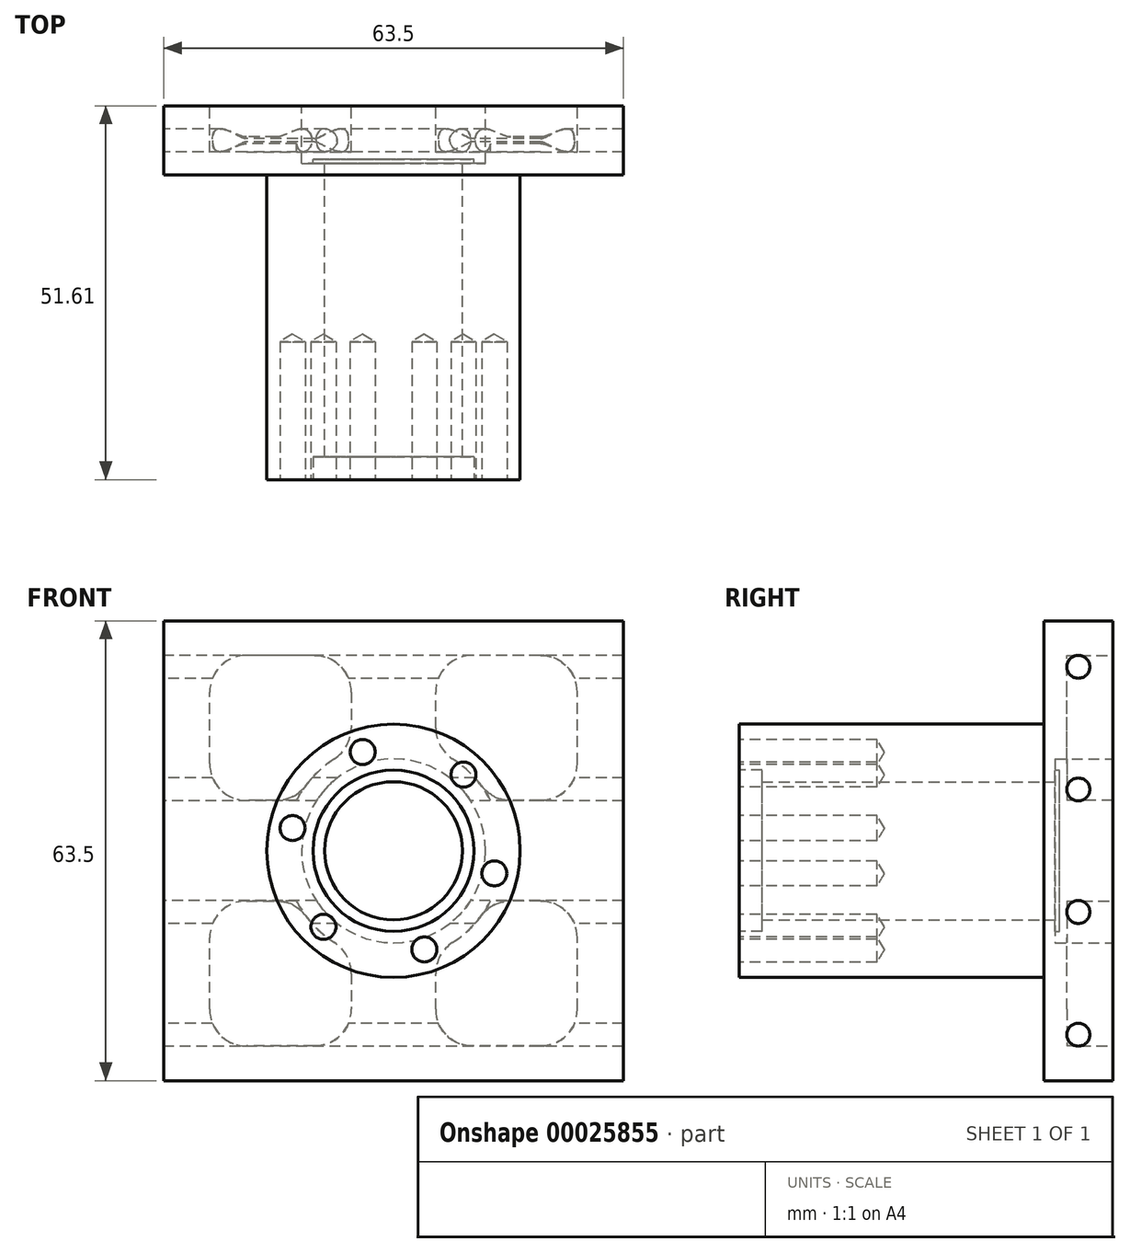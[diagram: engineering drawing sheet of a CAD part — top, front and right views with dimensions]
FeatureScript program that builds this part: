
annotation { "Feature Type Name" : "Feature", "Feature Type Description" : "" }
export const myFeature = defineFeature(function(context is Context, id is Id, definition is map)
    precondition{}
    {
        {
            var Q0;
            Q0=qCreatedBy(makeId("Front.planeOp"),FACE);
            var sketch = newSketch(context, id + "F0", { "sketchPlane" : qUnion([Q0])});
            skLineSegment(sketch, "E0.rect.bottom", {"start": v(31.75, -31.75) * mm, "end": v(-31.75, -31.75) * mm});
            skLineSegment(sketch, "E0.rect.top", {"start": v(31.75, 31.75) * mm, "end": v(-31.75, 31.75) * mm});
            skLineSegment(sketch, "E0.rect.left", {"start": v(31.75, -31.75) * mm, "end": v(31.75, 31.75) * mm});
            skLineSegment(sketch, "E0.rect.right", {"start": v(-31.75, -31.75) * mm, "end": v(-31.75, 31.75) * mm});
            skPoint(sketch, "E0.rect.middle", {"position": v(0, 0) * mm});
            skSolve(sketch);
        }
        {
            var Q0;
            Q0=makeQuery(id+"F0.imprint","IMPRINT",FACE,{"disambiguationData":[TD([[makeQuery(id+"F0.imprint","IMPRINT",EDGE,{"derivedFrom":sQuery(id+"F0.wireOp",EDGE,"E0.rect.bottom")}),-1.0]])]});
            extrude(context, id + "F1", {"entities" : qUnion([Q0]), "depth" : 9.52 * mm});
        }
        {
            var Q0;
            Q0=makeQuery(id+"F1.opExtrude","SWEPT_FACE",FACE,{"disambiguationData":[OSD([sQuery(id+"F0.wireOp",EDGE,"E0.rect.right")])]});
            var sketch = newSketch(context, id + "F2", { "sketchPlane" : qUnion([Q0])});
            skLineSegment(sketch, "E1", {"start": v(4.75, 47.41) * mm, "end": v(4.75, -43.38) * mm});
            skPoint(sketch, "E2", {"position": v(4.75, 25.4) * mm});
            skPoint(sketch, "E3", {"position": v(4.75, 8.46) * mm});
            skPoint(sketch, "E4", {"position": v(4.75, -8.46) * mm});
            skPoint(sketch, "E5", {"position": v(4.75, -25.4) * mm});
            skSolve(sketch);
        }
        {
            var Q0;
            Q0=sQuery(id+"F2.wireOp",VERTEX,"E2");
            var Q1;
            Q1=sQuery(id+"F2.wireOp",VERTEX,"E3");
            var Q2;
            Q2=sQuery(id+"F2.wireOp",VERTEX,"E4");
            var Q3;
            Q3=sQuery(id+"F2.wireOp",VERTEX,"E5");
            var Q4;
            Q4=makeQuery(id+"F1.opExtrude","SWEPT_BODY",BODY,{"disambiguationData":[OSD([sQuery(id+"F0.wireOp",EDGE,"E0.rect.bottom"),sQuery(id+"F0.wireOp",EDGE,"E0.rect.top"),sQuery(id+"F0.wireOp",EDGE,"E0.rect.left"),sQuery(id+"F0.wireOp",EDGE,"E0.rect.right")])]});
            hole(context, id + "F3", {"style" : HoleStyle.SIMPLE, "holeDiameter" : 3.17 * mm, "endStyle" : HoleEndStyle.THROUGH, "locations" : qUnion([Q0, Q1, Q2, Q3]), "scope" : qUnion([Q4])});
        }
        {
            var Q0;
            Q0=makeQuery(id+"F1.opExtrude","CAP_FACE",FACE,{"disambiguationData":[OSD([sQuery(id+"F0.wireOp",EDGE,"E0.rect.bottom"),sQuery(id+"F0.wireOp",EDGE,"E0.rect.top"),sQuery(id+"F0.wireOp",EDGE,"E0.rect.left"),sQuery(id+"F0.wireOp",EDGE,"E0.rect.right")])],"isStart":false});
            var sketch = newSketch(context, id + "F4", { "sketchPlane" : qUnion([Q0])});
            skCircle(sketch, "E6", {"center": v(0, 0) * mm, "radius": 17.49 * mm});
            skSolve(sketch);
        }
        {
            var Q0;
            Q0=makeQuery(id+"F4.imprint","IMPRINT",FACE,{"disambiguationData":[TD([[makeQuery(id+"F4.imprint","IMPRINT",EDGE,{"derivedFrom":sQuery(id+"F4.wireOp",EDGE,"E6")}),1.0]])]});
            extrude(context, id + "F5", {"entities" : qUnion([Q0]), "operationType" : NewBodyOperationType.ADD, "depth" : 42.1 * mm});
        }
        {
            var Q0;
            Q0=makeQuery(id+"F5.opExtrude","CAP_FACE",FACE,{"disambiguationData":[OSD([sQuery(id+"F4.wireOp",EDGE,"E6")])],"isStart":false});
            var sketch = newSketch(context, id + "F6", { "sketchPlane" : qUnion([Q0])});
            skCircle(sketch, "E7", {"center": v(0, 0) * mm, "radius": 14.29 * mm});
            skCircle(sketch, "E8.cCircle", {"center": v(0, 0) * mm, "radius": 14.29 * mm, "construction": true});
            skLineSegment(sketch, "E8.0", {"start": v(9.68, 10.51) * mm, "end": v(13.94, -3.12) * mm});
            skLineSegment(sketch, "E8.1", {"start": v(13.94, -3.12) * mm, "end": v(4.27, -13.64) * mm});
            skLineSegment(sketch, "E8.2", {"start": v(4.27, -13.64) * mm, "end": v(-9.68, -10.51) * mm});
            skLineSegment(sketch, "E8.3", {"start": v(-9.68, -10.51) * mm, "end": v(-13.94, 3.12) * mm});
            skLineSegment(sketch, "E8.4", {"start": v(-13.94, 3.12) * mm, "end": v(-4.27, 13.64) * mm});
            skLineSegment(sketch, "E8.5", {"start": v(-4.27, 13.64) * mm, "end": v(9.68, 10.51) * mm});
            skSolve(sketch);
        }
        {
            var Q0;
            Q0=sQuery(id+"F6.wireOp",VERTEX,"E8.3.end");
            var Q1;
            Q1=sQuery(id+"F6.wireOp",VERTEX,"E8.4.end");
            var Q2;
            Q2=sQuery(id+"F6.wireOp",VERTEX,"E8.0.start");
            var Q3;
            Q3=sQuery(id+"F6.wireOp",VERTEX,"E8.1.start");
            var Q4;
            Q4=sQuery(id+"F6.wireOp",VERTEX,"E8.2.start");
            var Q5;
            Q5=sQuery(id+"F6.wireOp",VERTEX,"E8.3.start");
            var Q6;
            Q6=makeQuery(id+"F1.opExtrude","SWEPT_BODY",BODY,{"disambiguationData":[OSD([sQuery(id+"F0.wireOp",EDGE,"E0.rect.bottom"),sQuery(id+"F0.wireOp",EDGE,"E0.rect.top"),sQuery(id+"F0.wireOp",EDGE,"E0.rect.left"),sQuery(id+"F0.wireOp",EDGE,"E0.rect.right")])]});
            hole(context, id + "F7", {"style" : HoleStyle.SIMPLE, "holeDiameter" : 3.45 * mm, "endStyle" : HoleEndStyle.BLIND, "holeDepth" : 19.05 * mm, "locations" : qUnion([Q0, Q1, Q2, Q3, Q4, Q5]), "scope" : qUnion([Q6])});
        }
        {
            var Q0;
            Q0=makeQuery(id+"F1.opExtrude","CAP_FACE",FACE,{"disambiguationData":[OSD([sQuery(id+"F0.wireOp",EDGE,"E0.rect.bottom"),sQuery(id+"F0.wireOp",EDGE,"E0.rect.top"),sQuery(id+"F0.wireOp",EDGE,"E0.rect.left"),sQuery(id+"F0.wireOp",EDGE,"E0.rect.right")])],"isStart":true});
            var sketch = newSketch(context, id + "F8", { "sketchPlane" : qUnion([Q0])});
            skCircle(sketch, "E9", {"center": v(0, 0) * mm, "radius": 12.7 * mm});
            skCircle(sketch, "E10", {"center": v(0, 0) * mm, "radius": 11.13 * mm});
            skCircle(sketch, "E11", {"center": v(0, 0) * mm, "radius": 9.53 * mm});
            skSolve(sketch);
        }
        {
            var Q0;
            Q0=makeQuery(id+"F8.imprint","IMPRINT",FACE,{"disambiguationData":[TD([[makeQuery(id+"F8.imprint","IMPRINT",EDGE,{"derivedFrom":sQuery(id+"F8.wireOp",EDGE,"E11")}),1.0]])]});
            extrude(context, id + "F9", {"entities" : qUnion([Q0]), "operationType" : NewBodyOperationType.REMOVE, "endBound" : BoundingType.THROUGH_ALL, "oppositeDirection" : true, "depth" : 25.4 * mm});
        }
        {
            var Q0;
            Q0=qCreatedBy(makeId("Front.planeOp"),FACE);
            var sketch = newSketch(context, id + "F10", { "sketchPlane" : qUnion([Q0])});
            skCircle(sketch, "E12", {"center": v(0, 0) * mm, "radius": 11.13 * mm});
            skCircle(sketch, "E13", {"center": v(0, 0) * mm, "radius": 12.7 * mm});
            skSolve(sketch);
        }
        {
            var Q0;
            Q0=makeQuery(id+"F10.imprint","IMPRINT",FACE,{"disambiguationData":[TD([[makeQuery(id+"F10.imprint","IMPRINT",EDGE,{"derivedFrom":sQuery(id+"F10.wireOp",EDGE,"E12")}),1.0]])]});
            extrude(context, id + "F11", {"entities" : qUnion([Q0]), "operationType" : NewBodyOperationType.REMOVE, "depth" : 7.37 * mm});
        }
        {
            var Q0;
            Q0=makeQuery(id+"F1.opExtrude","CAP_FACE",FACE,{"disambiguationData":[OSD([sQuery(id+"F0.wireOp",EDGE,"E0.rect.bottom"),sQuery(id+"F0.wireOp",EDGE,"E0.rect.top"),sQuery(id+"F0.wireOp",EDGE,"E0.rect.left"),sQuery(id+"F0.wireOp",EDGE,"E0.rect.right")])],"isStart":true});
            var sketch = newSketch(context, id + "F12", { "sketchPlane" : qUnion([Q0])});
            skCircle(sketch, "E14", {"center": v(0, 0) * mm, "radius": 12.7 * mm});
            skSolve(sketch);
        }
        {
            var Q0;
            Q0=makeQuery(id+"F12.imprint","IMPRINT",FACE,{"disambiguationData":[TD([[makeQuery(id+"F12.imprint","IMPRINT",EDGE,{"derivedFrom":sQuery(id+"F12.wireOp",EDGE,"E14")}),1.0]])]});
            extrude(context, id + "F13", {"entities" : qUnion([Q0]), "operationType" : NewBodyOperationType.REMOVE, "oppositeDirection" : true, "depth" : 7.95 * mm});
        }
        {
            var Q0;
            Q0=makeQuery(id+"F5.opExtrude","CAP_FACE",FACE,{"disambiguationData":[OSD([sQuery(id+"F4.wireOp",EDGE,"E6")])],"isStart":false});
            var sketch = newSketch(context, id + "F14", { "sketchPlane" : qUnion([Q0])});
            skCircle(sketch, "E15", {"center": v(0, 0) * mm, "radius": 11.13 * mm});
            skSolve(sketch);
        }
        {
            var Q0;
            Q0=makeQuery(id+"F14.imprint","IMPRINT",FACE,{"disambiguationData":[TD([[makeQuery(id+"F14.imprint","IMPRINT",EDGE,{"derivedFrom":sQuery(id+"F14.wireOp",EDGE,"E15")}),1.0]])]});
            extrude(context, id + "F15", {"entities" : qUnion([Q0]), "operationType" : NewBodyOperationType.REMOVE, "oppositeDirection" : true, "depth" : 3.17 * mm});
        }
        {
            var Q0;
            Q0=makeQuery(id+"F1.opExtrude","CAP_FACE",FACE,{"disambiguationData":[OSD([sQuery(id+"F0.wireOp",EDGE,"E0.rect.bottom"),sQuery(id+"F0.wireOp",EDGE,"E0.rect.top"),sQuery(id+"F0.wireOp",EDGE,"E0.rect.left"),sQuery(id+"F0.wireOp",EDGE,"E0.rect.right")])],"isStart":true});
            var sketch = newSketch(context, id + "F16", { "sketchPlane" : qUnion([Q0])});
            skLineSegment(sketch, "E16.rect.bottom", {"start": v(-25.4, -26.97) * mm, "end": v(25.4, -26.97) * mm});
            skLineSegment(sketch, "E16.rect.top", {"start": v(-25.4, 26.97) * mm, "end": v(25.4, 26.97) * mm});
            skLineSegment(sketch, "E16.rect.left", {"start": v(-25.4, -26.97) * mm, "end": v(-25.4, 26.97) * mm});
            skLineSegment(sketch, "E16.rect.right", {"start": v(25.4, -26.97) * mm, "end": v(25.4, 26.97) * mm});
            skPoint(sketch, "E16.rect.middle", {"position": v(0, 0) * mm});
            skCircle(sketch, "E17", {"center": v(0, 0) * mm, "radius": 15.09 * mm});
            skLineSegment(sketch, "E18", {"start": v(34.8, 0) * mm, "end": v(-37.6, 0) * mm});
            skLineSegment(sketch, "E19", {"start": v(25.4, 6.94) * mm, "end": v(13.4, 6.94) * mm});
            skLineSegment(sketch, "E20", {"start": v(25.4, -6.94) * mm, "end": v(13.4, -6.94) * mm});
            skLineSegment(sketch, "E21", {"start": v(-5.83, -26.97) * mm, "end": v(-5.83, -13.91) * mm});
            skLineSegment(sketch, "E22", {"start": v(5.83, 26.97) * mm, "end": v(5.83, 13.91) * mm});
            skPoint(sketch, "E23.start.orphan", {"position": v(0, -38.63) * mm});
            skLineSegment(sketch, "E24.trimOffspring", {"start": v(5.83, -13.91) * mm, "end": v(5.83, -26.97) * mm});
            skLineSegment(sketch, "E25.trimOffspring", {"start": v(-13.4, -6.94) * mm, "end": v(-25.4, -6.94) * mm});
            skLineSegment(sketch, "E26.trimOffspring", {"start": v(-13.4, 6.94) * mm, "end": v(-25.4, 6.94) * mm});
            skLineSegment(sketch, "E27.trimOffspring", {"start": v(-5.83, 13.91) * mm, "end": v(-5.83, 26.97) * mm});
            skSolve(sketch);
        }
        {
            var Q0;
            {var subQ1=sQuery(id+"F16.wireOp",EDGE,"E26.trimOffspring");Q0=makeQuery(id+"F16.imprint","IMPRINT",FACE,{"disambiguationData":[TD([[makeQuery(id+"F16.imprint","IMPRINT",EDGE,{"derivedFrom":subQ1}),-1.0]])]});}
            var Q1;
            {var subQ1=sQuery(id+"F16.wireOp",EDGE,"E21");Q1=makeQuery(id+"F16.imprint","IMPRINT",FACE,{"disambiguationData":[TD([[makeQuery(id+"F16.imprint","IMPRINT",EDGE,{"derivedFrom":subQ1}),1.0]])]});}
            var Q2;
            {var subQ0=sQuery(id+"F16.wireOp",EDGE,"E20");Q2=makeQuery(id+"F16.imprint","IMPRINT",FACE,{"disambiguationData":[TD([[makeQuery(id+"F16.imprint","IMPRINT",EDGE,{"derivedFrom":subQ0}),1.0]])]});}
            var Q3;
            {var subQ1=sQuery(id+"F16.wireOp",EDGE,"E19");Q3=makeQuery(id+"F16.imprint","IMPRINT",FACE,{"disambiguationData":[TD([[makeQuery(id+"F16.imprint","IMPRINT",EDGE,{"derivedFrom":subQ1}),-1.0]])]});}
            extrude(context, id + "F17", {"entities" : qUnion([Q0, Q1, Q2, Q3]), "operationType" : NewBodyOperationType.REMOVE, "oppositeDirection" : true, "depth" : 6.35 * mm});
        }
        {
            var Q0;
            {var subQ0=sQuery(id+"F16.wireOp",EDGE,"E16.rect.bottom");var subQ1=sQuery(id+"F16.wireOp",EDGE,"E24.trimOffspring");Q0=makeQuery(id+"F17.boolean.opBoolean","COPY",EDGE,{"disambiguationData":[TD([makeQuery(id+"F1.opExtrude","CAP_FACE",FACE,{"disambiguationData":[OSD([sQuery(id+"F0.wireOp",EDGE,"E0.rect.bottom"),sQuery(id+"F0.wireOp",EDGE,"E0.rect.top"),sQuery(id+"F0.wireOp",EDGE,"E0.rect.left"),sQuery(id+"F0.wireOp",EDGE,"E0.rect.right")])],"isStart":true})])],"derivedFrom":makeQuery(id+"F17.opExtrude","SWEPT_EDGE",EDGE,{"disambiguationData":[OSD([subQ0,subQ1])]})});}
            var Q1;
            {var subQ0=sQuery(id+"F16.wireOp",EDGE,"E16.rect.left");var subQ1=sQuery(id+"F16.wireOp",EDGE,"E16.rect.bottom");Q1=makeQuery(id+"F17.boolean.opBoolean","COPY",EDGE,{"disambiguationData":[TD([makeQuery(id+"F1.opExtrude","CAP_FACE",FACE,{"disambiguationData":[OSD([sQuery(id+"F0.wireOp",EDGE,"E0.rect.bottom"),sQuery(id+"F0.wireOp",EDGE,"E0.rect.top"),sQuery(id+"F0.wireOp",EDGE,"E0.rect.left"),sQuery(id+"F0.wireOp",EDGE,"E0.rect.right")])],"isStart":true})])],"derivedFrom":makeQuery(id+"F17.opExtrude","SWEPT_EDGE",EDGE,{"disambiguationData":[OSD([subQ1,subQ0])]})});}
            var Q2;
            {var subQ0=sQuery(id+"F16.wireOp",EDGE,"E26.trimOffspring");var subQ1=sQuery(id+"F16.wireOp",EDGE,"E16.rect.left");Q2=makeQuery(id+"F17.boolean.opBoolean","COPY",EDGE,{"disambiguationData":[TD([makeQuery(id+"F1.opExtrude","CAP_FACE",FACE,{"disambiguationData":[OSD([sQuery(id+"F0.wireOp",EDGE,"E0.rect.bottom"),sQuery(id+"F0.wireOp",EDGE,"E0.rect.top"),sQuery(id+"F0.wireOp",EDGE,"E0.rect.left"),sQuery(id+"F0.wireOp",EDGE,"E0.rect.right")])],"isStart":true})])],"derivedFrom":makeQuery(id+"F17.opExtrude","SWEPT_EDGE",EDGE,{"disambiguationData":[OSD([subQ1,subQ0])]})});}
            var Q3;
            Q3=makeQuery(id+"F17.boolean.opBoolean","COPY",EDGE,{"derivedFrom":makeQuery(id+"F17.opExtrude","SWEPT_EDGE",EDGE,{"disambiguationData":[OSD([sQuery(id+"F16.wireOp",EDGE,"E17"),sQuery(id+"F16.wireOp",EDGE,"E22")])]})});
            var Q4;
            {var subQ0=sQuery(id+"F16.wireOp",EDGE,"E19");var subQ1=sQuery(id+"F16.wireOp",EDGE,"E17");Q4=makeQuery(id+"F17.boolean.opBoolean","COPY",EDGE,{"disambiguationData":[TD([makeQuery(id+"F1.opExtrude","CAP_FACE",FACE,{"disambiguationData":[OSD([sQuery(id+"F0.wireOp",EDGE,"E0.rect.bottom"),sQuery(id+"F0.wireOp",EDGE,"E0.rect.top"),sQuery(id+"F0.wireOp",EDGE,"E0.rect.left"),sQuery(id+"F0.wireOp",EDGE,"E0.rect.right")])],"isStart":true})])],"derivedFrom":makeQuery(id+"F17.opExtrude","SWEPT_EDGE",EDGE,{"disambiguationData":[OSD([subQ1,subQ0])]})});}
            var Q5;
            {var subQ0=sQuery(id+"F16.wireOp",EDGE,"E16.rect.left");var subQ1=sQuery(id+"F16.wireOp",EDGE,"E16.rect.top");Q5=makeQuery(id+"F17.boolean.opBoolean","COPY",EDGE,{"disambiguationData":[TD([makeQuery(id+"F1.opExtrude","CAP_FACE",FACE,{"disambiguationData":[OSD([sQuery(id+"F0.wireOp",EDGE,"E0.rect.bottom"),sQuery(id+"F0.wireOp",EDGE,"E0.rect.top"),sQuery(id+"F0.wireOp",EDGE,"E0.rect.left"),sQuery(id+"F0.wireOp",EDGE,"E0.rect.right")])],"isStart":true})])],"derivedFrom":makeQuery(id+"F17.opExtrude","SWEPT_EDGE",EDGE,{"disambiguationData":[OSD([subQ1,subQ0])]})});}
            var Q6;
            {var subQ0=sQuery(id+"F16.wireOp",EDGE,"E16.rect.top");var subQ1=sQuery(id+"F16.wireOp",EDGE,"E22");Q6=makeQuery(id+"F17.boolean.opBoolean","COPY",EDGE,{"disambiguationData":[TD([makeQuery(id+"F1.opExtrude","CAP_FACE",FACE,{"disambiguationData":[OSD([sQuery(id+"F0.wireOp",EDGE,"E0.rect.bottom"),sQuery(id+"F0.wireOp",EDGE,"E0.rect.top"),sQuery(id+"F0.wireOp",EDGE,"E0.rect.left"),sQuery(id+"F0.wireOp",EDGE,"E0.rect.right")])],"isStart":true})])],"derivedFrom":makeQuery(id+"F17.opExtrude","SWEPT_EDGE",EDGE,{"disambiguationData":[OSD([subQ0,subQ1])]})});}
            var Q7;
            {var subQ0=sQuery(id+"F16.wireOp",EDGE,"E20");var subQ1=sQuery(id+"F16.wireOp",EDGE,"E17");Q7=makeQuery(id+"F17.boolean.opBoolean","COPY",EDGE,{"disambiguationData":[TD([makeQuery(id+"F1.opExtrude","CAP_FACE",FACE,{"disambiguationData":[OSD([sQuery(id+"F0.wireOp",EDGE,"E0.rect.bottom"),sQuery(id+"F0.wireOp",EDGE,"E0.rect.top"),sQuery(id+"F0.wireOp",EDGE,"E0.rect.left"),sQuery(id+"F0.wireOp",EDGE,"E0.rect.right")])],"isStart":true})])],"derivedFrom":makeQuery(id+"F17.opExtrude","SWEPT_EDGE",EDGE,{"disambiguationData":[OSD([subQ1,subQ0])]})});}
            var Q8;
            Q8=makeQuery(id+"F17.boolean.opBoolean","COPY",EDGE,{"derivedFrom":makeQuery(id+"F17.opExtrude","SWEPT_EDGE",EDGE,{"disambiguationData":[OSD([sQuery(id+"F16.wireOp",EDGE,"E17"),sQuery(id+"F16.wireOp",EDGE,"E24.trimOffspring")])]})});
            var Q9;
            {var subQ0=sQuery(id+"F16.wireOp",EDGE,"E16.rect.left");var subQ1=sQuery(id+"F16.wireOp",EDGE,"E25.trimOffspring");Q9=makeQuery(id+"F17.boolean.opBoolean","COPY",EDGE,{"disambiguationData":[TD([makeQuery(id+"F1.opExtrude","CAP_FACE",FACE,{"disambiguationData":[OSD([sQuery(id+"F0.wireOp",EDGE,"E0.rect.bottom"),sQuery(id+"F0.wireOp",EDGE,"E0.rect.top"),sQuery(id+"F0.wireOp",EDGE,"E0.rect.left"),sQuery(id+"F0.wireOp",EDGE,"E0.rect.right")])],"isStart":true})])],"derivedFrom":makeQuery(id+"F17.opExtrude","SWEPT_EDGE",EDGE,{"disambiguationData":[OSD([subQ0,subQ1])]})});}
            var Q10;
            {var subQ0=sQuery(id+"F16.wireOp",EDGE,"E16.rect.right");var subQ1=sQuery(id+"F16.wireOp",EDGE,"E16.rect.bottom");Q10=makeQuery(id+"F17.boolean.opBoolean","COPY",EDGE,{"disambiguationData":[TD([makeQuery(id+"F1.opExtrude","CAP_FACE",FACE,{"disambiguationData":[OSD([sQuery(id+"F0.wireOp",EDGE,"E0.rect.bottom"),sQuery(id+"F0.wireOp",EDGE,"E0.rect.top"),sQuery(id+"F0.wireOp",EDGE,"E0.rect.left"),sQuery(id+"F0.wireOp",EDGE,"E0.rect.right")])],"isStart":true})])],"derivedFrom":makeQuery(id+"F17.opExtrude","SWEPT_EDGE",EDGE,{"disambiguationData":[OSD([subQ1,subQ0])]})});}
            var Q11;
            {var subQ0=sQuery(id+"F16.wireOp",EDGE,"E16.rect.right");var subQ1=sQuery(id+"F16.wireOp",EDGE,"E20");Q11=makeQuery(id+"F17.boolean.opBoolean","COPY",EDGE,{"disambiguationData":[TD([makeQuery(id+"F1.opExtrude","CAP_FACE",FACE,{"disambiguationData":[OSD([sQuery(id+"F0.wireOp",EDGE,"E0.rect.bottom"),sQuery(id+"F0.wireOp",EDGE,"E0.rect.top"),sQuery(id+"F0.wireOp",EDGE,"E0.rect.left"),sQuery(id+"F0.wireOp",EDGE,"E0.rect.right")])],"isStart":true})])],"derivedFrom":makeQuery(id+"F17.opExtrude","SWEPT_EDGE",EDGE,{"disambiguationData":[OSD([subQ0,subQ1])]})});}
            var Q12;
            {var subQ0=sQuery(id+"F16.wireOp",EDGE,"E16.rect.right");var subQ1=sQuery(id+"F16.wireOp",EDGE,"E16.rect.top");Q12=makeQuery(id+"F17.boolean.opBoolean","COPY",EDGE,{"disambiguationData":[TD([makeQuery(id+"F1.opExtrude","CAP_FACE",FACE,{"disambiguationData":[OSD([sQuery(id+"F0.wireOp",EDGE,"E0.rect.bottom"),sQuery(id+"F0.wireOp",EDGE,"E0.rect.top"),sQuery(id+"F0.wireOp",EDGE,"E0.rect.left"),sQuery(id+"F0.wireOp",EDGE,"E0.rect.right")])],"isStart":true})])],"derivedFrom":makeQuery(id+"F17.opExtrude","SWEPT_EDGE",EDGE,{"disambiguationData":[OSD([subQ1,subQ0])]})});}
            var Q13;
            {var subQ0=sQuery(id+"F16.wireOp",EDGE,"E16.rect.right");var subQ1=sQuery(id+"F16.wireOp",EDGE,"E19");Q13=makeQuery(id+"F17.boolean.opBoolean","COPY",EDGE,{"disambiguationData":[TD([makeQuery(id+"F1.opExtrude","CAP_FACE",FACE,{"disambiguationData":[OSD([sQuery(id+"F0.wireOp",EDGE,"E0.rect.bottom"),sQuery(id+"F0.wireOp",EDGE,"E0.rect.top"),sQuery(id+"F0.wireOp",EDGE,"E0.rect.left"),sQuery(id+"F0.wireOp",EDGE,"E0.rect.right")])],"isStart":true})])],"derivedFrom":makeQuery(id+"F17.opExtrude","SWEPT_EDGE",EDGE,{"disambiguationData":[OSD([subQ0,subQ1])]})});}
            var Q14;
            Q14=makeQuery(id+"F17.boolean.opBoolean","COPY",EDGE,{"derivedFrom":makeQuery(id+"F17.opExtrude","SWEPT_EDGE",EDGE,{"disambiguationData":[OSD([sQuery(id+"F16.wireOp",EDGE,"E17"),sQuery(id+"F16.wireOp",EDGE,"E27.trimOffspring")])]})});
            var Q15;
            {var subQ0=sQuery(id+"F16.wireOp",EDGE,"E26.trimOffspring");var subQ1=sQuery(id+"F16.wireOp",EDGE,"E17");Q15=makeQuery(id+"F17.boolean.opBoolean","COPY",EDGE,{"disambiguationData":[TD([makeQuery(id+"F1.opExtrude","CAP_FACE",FACE,{"disambiguationData":[OSD([sQuery(id+"F0.wireOp",EDGE,"E0.rect.bottom"),sQuery(id+"F0.wireOp",EDGE,"E0.rect.top"),sQuery(id+"F0.wireOp",EDGE,"E0.rect.left"),sQuery(id+"F0.wireOp",EDGE,"E0.rect.right")])],"isStart":true})])],"derivedFrom":makeQuery(id+"F17.opExtrude","SWEPT_EDGE",EDGE,{"disambiguationData":[OSD([subQ1,subQ0])]})});}
            var Q16;
            {var subQ0=sQuery(id+"F16.wireOp",EDGE,"E16.rect.bottom");var subQ1=sQuery(id+"F16.wireOp",EDGE,"E21");Q16=makeQuery(id+"F17.boolean.opBoolean","COPY",EDGE,{"disambiguationData":[TD([makeQuery(id+"F1.opExtrude","CAP_FACE",FACE,{"disambiguationData":[OSD([sQuery(id+"F0.wireOp",EDGE,"E0.rect.bottom"),sQuery(id+"F0.wireOp",EDGE,"E0.rect.top"),sQuery(id+"F0.wireOp",EDGE,"E0.rect.left"),sQuery(id+"F0.wireOp",EDGE,"E0.rect.right")])],"isStart":true})])],"derivedFrom":makeQuery(id+"F17.opExtrude","SWEPT_EDGE",EDGE,{"disambiguationData":[OSD([subQ0,subQ1])]})});}
            var Q17;
            Q17=makeQuery(id+"F17.boolean.opBoolean","COPY",EDGE,{"derivedFrom":makeQuery(id+"F17.opExtrude","SWEPT_EDGE",EDGE,{"disambiguationData":[OSD([sQuery(id+"F16.wireOp",EDGE,"E17"),sQuery(id+"F16.wireOp",EDGE,"E21")])]})});
            var Q18;
            {var subQ0=sQuery(id+"F16.wireOp",EDGE,"E17");var subQ1=sQuery(id+"F16.wireOp",EDGE,"E25.trimOffspring");Q18=makeQuery(id+"F17.boolean.opBoolean","COPY",EDGE,{"disambiguationData":[TD([makeQuery(id+"F1.opExtrude","CAP_FACE",FACE,{"disambiguationData":[OSD([sQuery(id+"F0.wireOp",EDGE,"E0.rect.bottom"),sQuery(id+"F0.wireOp",EDGE,"E0.rect.top"),sQuery(id+"F0.wireOp",EDGE,"E0.rect.left"),sQuery(id+"F0.wireOp",EDGE,"E0.rect.right")])],"isStart":true})])],"derivedFrom":makeQuery(id+"F17.opExtrude","SWEPT_EDGE",EDGE,{"disambiguationData":[OSD([subQ0,subQ1])]})});}
            var Q19;
            {var subQ0=sQuery(id+"F16.wireOp",EDGE,"E16.rect.top");var subQ1=sQuery(id+"F16.wireOp",EDGE,"E27.trimOffspring");Q19=makeQuery(id+"F17.boolean.opBoolean","COPY",EDGE,{"disambiguationData":[TD([makeQuery(id+"F1.opExtrude","CAP_FACE",FACE,{"disambiguationData":[OSD([sQuery(id+"F0.wireOp",EDGE,"E0.rect.bottom"),sQuery(id+"F0.wireOp",EDGE,"E0.rect.top"),sQuery(id+"F0.wireOp",EDGE,"E0.rect.left"),sQuery(id+"F0.wireOp",EDGE,"E0.rect.right")])],"isStart":true})])],"derivedFrom":makeQuery(id+"F17.opExtrude","SWEPT_EDGE",EDGE,{"disambiguationData":[OSD([subQ0,subQ1])]})});}
            fillet(context, id + "F18", {"entities" : qUnion([Q0, Q1, Q2, Q3, Q4, Q5, Q6, Q7, Q8, Q9, Q10, Q11, Q12, Q13, Q14, Q15, Q16, Q17, Q18, Q19]), "radius" : 5.08 * mm, "tangentPropagation" : true, "allowEdgeOverflow" : false});
        }
    });
